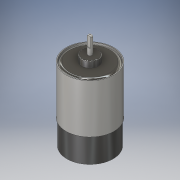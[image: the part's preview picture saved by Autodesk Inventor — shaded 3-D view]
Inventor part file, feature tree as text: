
AUTODESK INVENTOR PART (.ipt)
format: ipt  version: 2016 (Build 200138000, 138)  size: 176,640 bytes
history: native  units: in
note: dims shown in document units (in); Inventor stores cm internally (conversion verified against a paired STEP export)
features: extrude x5, sketch x5, fillet x3
ambient origin geometry x8: Origin, YZ Plane, XZ Plane, XY Plane, X Axis, Y Axis, Z Axis, Center Point
bodies: Solid1 (feature_tree)
feature tree (13):
  extrude  "Extrusion1"  Depth=2.23in TaperAngle=0.0deg
  extrude  "Extrusion2"  Depth=0.19in TaperAngle=0.0deg
  extrude  "Extrusion3"  Depth=0.2in TaperAngle=0.0deg
  extrude  "Extrusion4"  Depth=0.05in
  fillet  "Fillet1"  Radius=0.1in
  fillet  "Fillet2"  Radius=0.02in
  fillet  "Fillet3"  Radius=1.41in
  extrude  "Extrusion5"  Depth=1.488in TaperAngle=0.0deg
  sketch  "Sketch1"  dims[d0=1.41in d1=2.23in d2=0.0in]
  sketch  "Sketch2"  dims[d3=0.515in d4=0.19in d5=0.0in]
  sketch  "Sketch3"  dims[d6=0.128in d7=0.2in d8=0.0in]
  sketch  "Sketch4"  dims[d11=0.32in d12=0.0in d13=0.05in d14=0.1in d15=0.02in d17=1.41in]
  sketch  "Sketch5"  dims[d18=0.025in d19=1.488in d20=0.0in]
